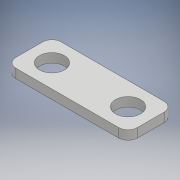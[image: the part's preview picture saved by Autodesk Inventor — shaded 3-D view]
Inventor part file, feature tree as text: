
AUTODESK INVENTOR PART (.ipt)
format: ipt  version: 2018 (Build 220112000, 112)  size: 117,760 bytes
history: native  units: mm
features: extrude x2, sketch x1, mirror x1, fillet x1
ambient origin geometry x8: Origin, YZ Plane, XZ Plane, XY Plane, X Axis, Y Axis, Z Axis, Center Point
bodies: Solid1 (feature_tree)
feature tree (5):
  sketch  "Sketch1"  dims[d3=45.0mm d4=22.0mm d6=8.0mm d7=0.0mm d8=10.0mm d9=0.0mm d10=8.25mm d11=20.0mm d12=20.0mm]
  extrude  "Extrusion1"  Depth=8.25mm
  extrude  "Extrusion2"  Depth=8.0mm TaperAngle=0.0deg
  mirror  "Mirror1"
  fillet  "Fillet1"  Radius=10.0mm
